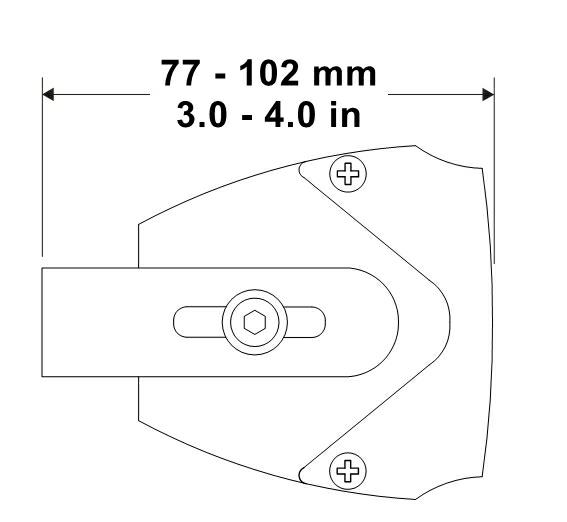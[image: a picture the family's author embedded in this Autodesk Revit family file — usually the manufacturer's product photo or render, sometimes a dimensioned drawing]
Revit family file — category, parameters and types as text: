
# Revit family: Electronics_Desono_Biamp_Two-Way-Column-Loudspeaker_COLW41
name_source: partatom
category: Communication Devices
units: mm (PartAtom-declared; Revit-internal decimal feet)

## family parameters
Cut with Voids When Loaded = No
Host = Face
Maintain Annotation Orientation = No
OmniClass Number = 23.85.10.11.14.14.14
OmniClass Title = Loudspeakers
Part Type = Normal
Room Calculation Point = No
Round Connector Dimension = Use Diameter
Shared = No

## types (1)
- COLW41
    Bracket Material = Biamp - Metal - White
    Connector Description = Terminal block; Low impedance 16 ohms; 70V/100V operation
    Continuous Power Handling Nominal Impedance = 25V; 40W @ 16Ω (160W peak)
    Controls = None; select transformer tap or low impedance input via terminal block wiring
    Default Elevation = 4' - 0"
    Depth = 0' - 3 1/2"
    Description = Desono™ COLW41 Two-Way 4 x 3.3 Column Loudspeaker
    Environmental = IP66 per IEC 60529
    Grill Material = Biamp - Plastic - White(Grid)
    Height = 1' - 10"
    Housing Material = Biamp - Plastic - White
    Input Connection = Multi-position pass-through, screw-down terminal block
    Manufacturer = Biamp
    Model = COLW41
    Mounting Provisions = Adjustable tilt L-bracket
    Nominal Beamwidth (H x V) = 100° x 15°
    Nominal Maximum SPL @ 1m = Peak - 116dB; Continuous - 110dB
    Nominal Sensitivity @ 1m = 1W - 94dB; 2.83V - 91dB
    Operating Environment = Indoor/Outdoor
    Operating Mode = Passive
    Operating Range (-10dB) = 155 Hz to 16 kHz
    Product Documentation Link = https://downloads.biamp.com
    Product Page URL = https://www.biamp.com
    Product data url = https://www.bimobject.com
    Recommended Amplifers = 40W - 80W @ 16Ω (25V - 36V)
    Shipping Weight = 9.20 lb
    Transducers = LF 4 x 3.3 (84 mm) coated paper cone HF 1 x 1 (25 mm) soft dome
    Transformer = 70V: 40W, 20W, 15W, 7.5W; 100V: 40W, 30W, 15W
    URL = https://www.biamp.com
    Weight = 8.60 lb
    Width = 0' - 4"

## geometry (parser evidence)
native form markers: Sweep x5
no freeform markers — native parametric forms only
